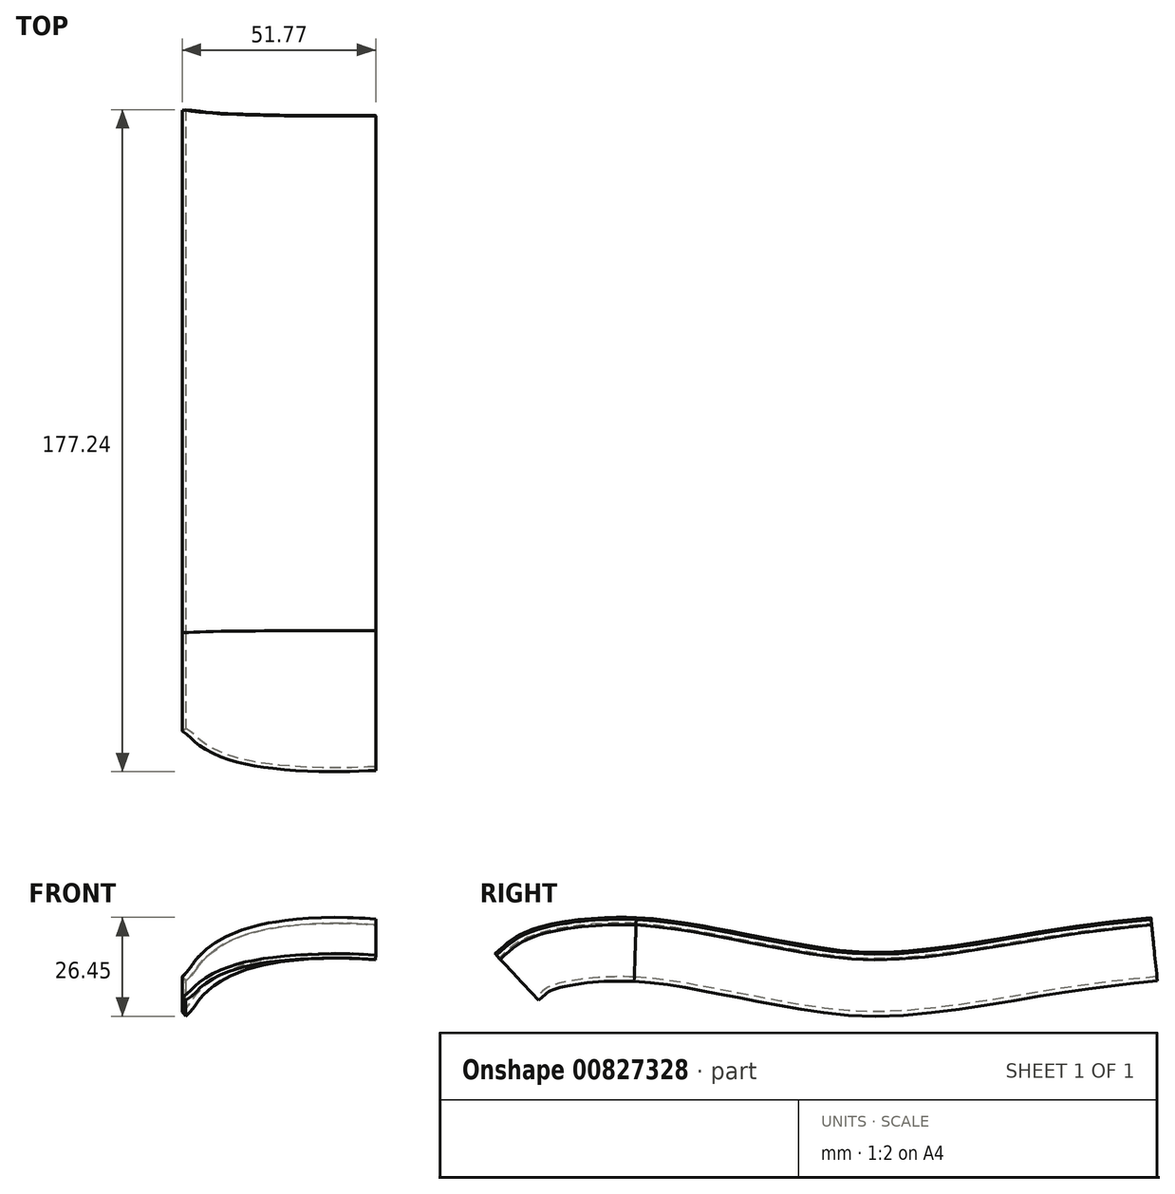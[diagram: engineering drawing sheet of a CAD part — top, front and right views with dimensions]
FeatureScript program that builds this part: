
annotation { "Feature Type Name" : "Feature", "Feature Type Description" : "" }
export const myFeature = defineFeature(function(context is Context, id is Id, definition is map)
    precondition{}
    {
        {
            var Q0;
            Q0=qCreatedBy(makeId("Right.planeOp"),FACE);
            var sketch = newSketch(context, id + "F0", { "sketchPlane" : qUnion([Q0])});
            skFitSpline(sketch, "E0", {"points": [v(65.57, -0.1) * mm, v(42.98, -2.77) * mm, v(15.63, -7.22) * mm, v(-9.5, -9.45) * mm, v(-27.17, -7.47) * mm, v(-43.85, -4.36) * mm, v(-56.7, -1.94) * mm, v(-72.16, -0.1) * mm], "startDerivative": vector(-144.93, -14.74) * mm, "endDerivative": vector(-117, 5.33) * mm});
            skFitSpline(sketch, "E1", {"points": [v(-72.16, -0.1) * mm, v(-79.71, -0.1) * mm, v(-91.54, -1.22) * mm, v(-103.36, -4.72) * mm, v(-110.08, -9.87) * mm], "startDerivative": vector(-32.8, 0.6) * mm, "endDerivative": vector(-26.07, -24.24) * mm});
            skSolve(sketch);
        }
        {
            var Q0;
            Q0=sQuery(id+"F0.wireOp",VERTEX,"E0.start");
            var Q1;
            Q1=sQuery(id+"F0.wireOp",EDGE,"E0");
            cPlane(context, id + "F1", {"entities" : qUnion([Q0, Q1]), "cplaneType" : CPlaneType.CURVE_POINT, "offset" : 25 * mm, "width" : 150 * mm, "height" : 150 * mm});
        }
        {
            var Q0;
            Q0=qCreatedBy(id+"F1.planeOp",FACE);
            var sketch = newSketch(context, id + "F2", { "sketchPlane" : qUnion([Q0])});
            skFitSpline(sketch, "E2", {"points": [v(18.2, -8.96) * mm, v(10.88, -8.52) * mm, v(-1.55, -8.85) * mm, v(-13.2, -10.64) * mm, v(-21.2, -13.54) * mm, v(-28.19, -18.78) * mm, v(-32.5, -24.03) * mm], "startDerivative": vector(-46.3, 3.75) * mm, "endDerivative": vector(-40.83, -32.86) * mm});
            skPoint(sketch, "E3.end.orphan", {"position": v(32.5, -10.53) * mm});
            skFitSpline(sketch, "E4.0", {"points": [v(18.33, -7.47) * mm, v(17.37, -7.4) * mm, v(15.93, -7.27) * mm, v(13.9, -7.14) * mm, v(12.28, -7.06) * mm, v(10.55, -7) * mm, v(8.68, -6.98) * mm, v(6.72, -6.98) * mm, v(3.98, -7.03) * mm, v(1.15, -7.15) * mm, v(-1.69, -7.35) * mm, v(-4.48, -7.61) * mm, v(-7.2, -7.96) * mm, v(-9.8, -8.4) * mm, v(-11.68, -8.75) * mm, v(-13.48, -9.15) * mm, v(-15.2, -9.59) * mm, v(-16.84, -10.08) * mm, v(-18.45, -10.64) * mm, v(-20.02, -11.3) * mm, v(-21.59, -12.04) * mm, v(-23.16, -12.9) * mm, v(-24.71, -13.86) * mm, v(-26.21, -14.91) * mm, v(-27.61, -16.06) * mm, v(-28.67, -17.07) * mm, v(-29.44, -17.92) * mm, v(-29.95, -18.57) * mm, v(-30.41, -19.2) * mm, v(-30.98, -20) * mm, v(-31.64, -20.95) * mm, v(-32.45, -21.96) * mm, v(-33.08, -22.57) * mm, v(-33.44, -22.86) * mm]});
            skLineSegment(sketch, "E5", {"start": v(18.33, -7.47) * mm, "end": v(18.2, -8.96) * mm});
            skLineSegment(sketch, "E6", {"start": v(-33.44, -22.86) * mm, "end": v(-32.5, -24.03) * mm});
            skSolve(sketch);
        }
        {
            var Q0;
            Q0=qSketchRegion(id+"F2",true);
            var Q1;
            Q1=sQuery(id+"F0.wireOp",EDGE,"E0");
            var Q2;
            Q2=sQuery(id+"F0.wireOp",EDGE,"E1");
            sweep(context, id + "F3", {"profiles" : qUnion([Q0]), "path" : qUnion([Q1, Q2])});
        }
    });
